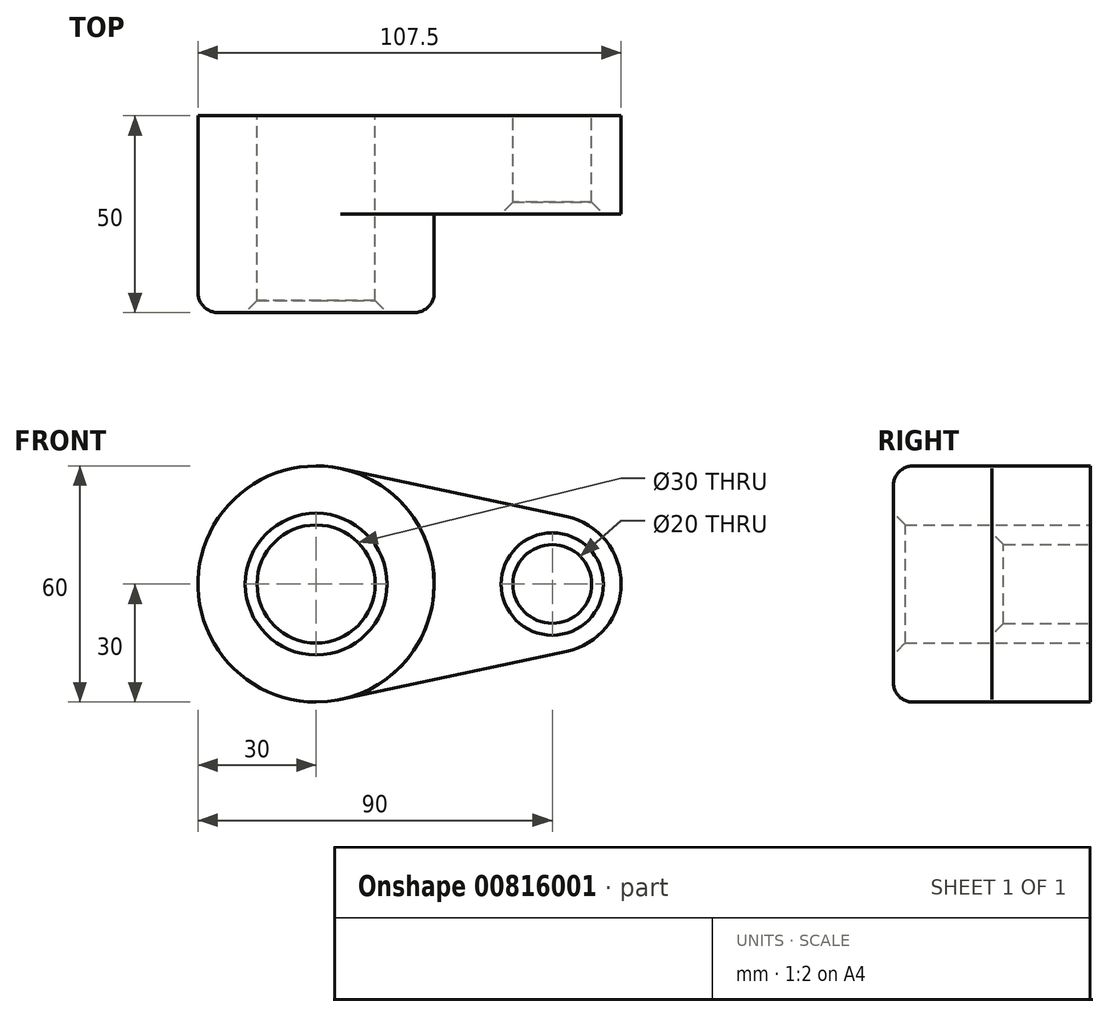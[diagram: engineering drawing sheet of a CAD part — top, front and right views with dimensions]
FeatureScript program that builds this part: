
annotation { "Feature Type Name" : "Feature", "Feature Type Description" : "" }
export const myFeature = defineFeature(function(context is Context, id is Id, definition is map)
    precondition{}
    {
        {
            var Q0;
            Q0=qCreatedBy(makeId("Front.planeOp"),FACE);
            var sketch = newSketch(context, id + "F0", { "sketchPlane" : qUnion([Q0])});
            skCircle(sketch, "E0", {"center": v(0, 0) * mm, "radius": 30 * mm});
            skCircle(sketch, "E1", {"center": v(60, 0) * mm, "radius": 17.5 * mm});
            skCircle(sketch, "E2", {"center": v(0, 0) * mm, "radius": 15 * mm});
            skCircle(sketch, "E3", {"center": v(60, 0) * mm, "radius": 10 * mm});
            skLineSegment(sketch, "E4", {"start": v(6.25, 29.34) * mm, "end": v(63.65, 17.12) * mm});
            skLineSegment(sketch, "E5", {"start": v(6.25, -29.34) * mm, "end": v(63.65, -17.12) * mm});
            skSolve(sketch);
        }
        {
            var Q0;
            Q0 = qSketchRegion(id + "F0", true);
            extrude(context, id + "F1", {"entities" : qUnion([Q0]), "depth" : 25 * mm, "offsetDistance" : 25 * mm});
        }
        {
            var Q0;
            Q0=makeQuery(id+"F0.imprint","IMPRINT",FACE,{"disambiguationData":[TD([[makeQuery(id+"F0.imprint","IMPRINT",EDGE,{"derivedFrom":sQuery(id+"F0.wireOp",EDGE,"E2")}),-1.0]])]});
            extrude(context, id + "F2", {"entities" : qUnion([Q0]), "operationType" : NewBodyOperationType.ADD, "depth" : 50 * mm, "offsetDistance" : 25 * mm});
        }
        {
            var Q0;
            Q0=makeQuery(id+"F2.opExtrude","CAP_EDGE",EDGE,{"disambiguationData":[OSD([sQuery(id+"F0.wireOp",EDGE,"E0")])],"isStart":false});
            fillet(context, id + "F3", {"entities" : qUnion([Q0]), "radius" : 5 * mm, "tangentPropagation" : true, "allowEdgeOverflow" : false});
        }
        {
            var Q0;
            Q0=makeQuery(id+"F2.opExtrude","CAP_EDGE",EDGE,{"disambiguationData":[OSD([sQuery(id+"F0.wireOp",EDGE,"E2")])],"isStart":false});
            var Q1;
            Q1=makeQuery(id+"F1.opExtrude","CAP_EDGE",EDGE,{"disambiguationData":[OSD([sQuery(id+"F0.wireOp",EDGE,"E3")])],"isStart":false});
            chamfer(context, id + "F4", {"entities" : qUnion([Q0, Q1]), "width" : 3 * mm, "tangentPropagation" : true});
        }
    });
